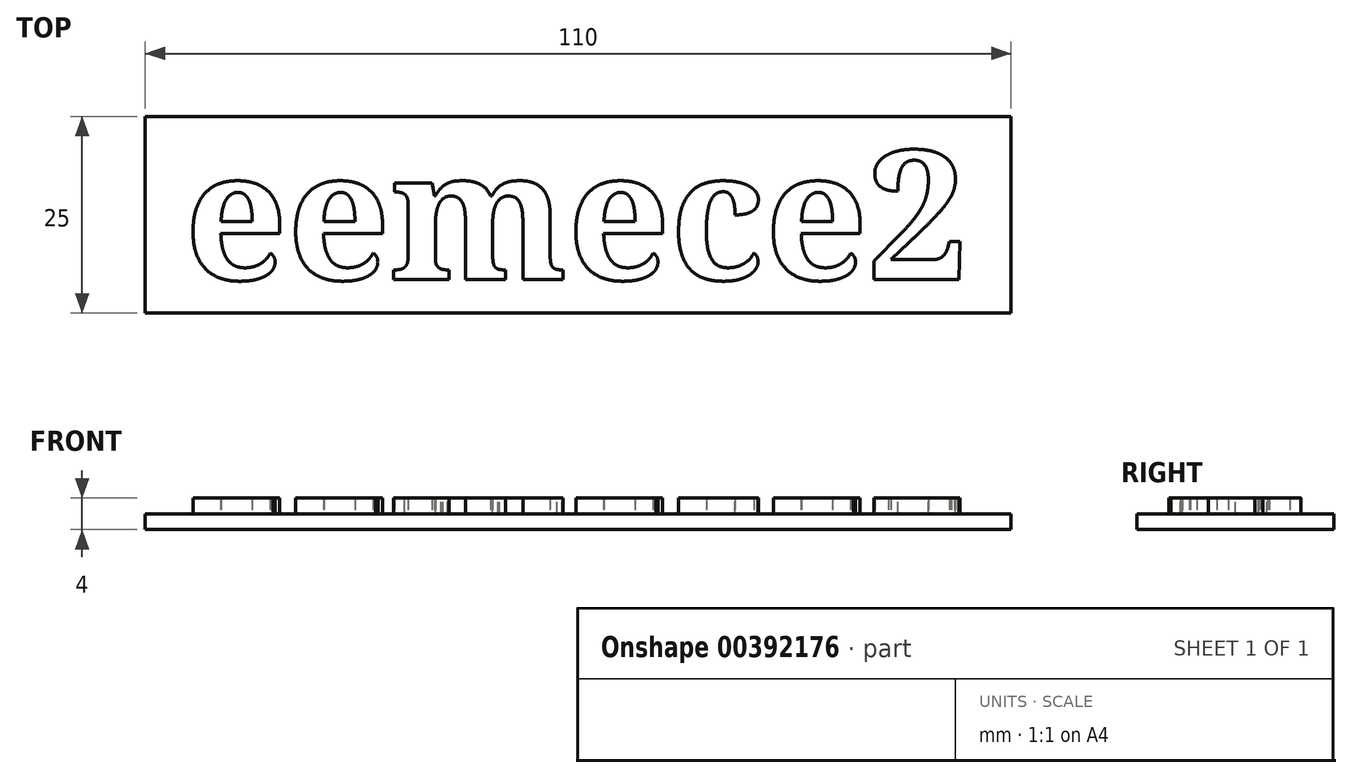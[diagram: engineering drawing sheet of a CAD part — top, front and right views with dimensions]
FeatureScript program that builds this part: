
annotation { "Feature Type Name" : "Feature", "Feature Type Description" : "" }
export const myFeature = defineFeature(function(context is Context, id is Id, definition is map)
    precondition{}
    {
        {
            var Q0;
            Q0=qCreatedBy(makeId("Top.planeOp"),FACE);
            var sketch = newSketch(context, id + "F0", { "sketchPlane" : qUnion([Q0])});
            skLineSegment(sketch, "E0.bottom", {"start": v(-55, 12.5) * mm, "end": v(55, 12.5) * mm});
            skLineSegment(sketch, "E0.top", {"start": v(-55, -12.5) * mm, "end": v(55, -12.5) * mm});
            skLineSegment(sketch, "E0.left", {"start": v(-55, 12.5) * mm, "end": v(-55, -12.5) * mm});
            skLineSegment(sketch, "E0.right", {"start": v(55, 12.5) * mm, "end": v(55, -12.5) * mm});
            skSolve(sketch);
        }
        {
            var Q0;
            Q0 = qSketchRegion(id + "F0", true);
            extrude(context, id + "F1", {"entities" : qUnion([Q0]), "depth" : 2 * mm});
        }
        {
            var Q0;
            Q0=makeQuery(id+"F1.opExtrude","CAP_FACE",FACE,{"disambiguationData":[OSD([sQuery(id+"F0.wireOp",EDGE,"E0.bottom"),sQuery(id+"F0.wireOp",EDGE,"E0.top"),sQuery(id+"F0.wireOp",EDGE,"E0.left"),sQuery(id+"F0.wireOp",EDGE,"E0.right")])],"isStart":false});
            var sketch = newSketch(context, id + "F2", { "sketchPlane" : qUnion([Q0])});
            skText(sketch, "E1", { "text": "eemece2", "fontName": "NotoSerif-Bold.ttf"});
            const initialGuessF2  = {"E1": [-0.05, -0.00823, 1, 0, 0.01646]};
            skSetInitialGuess(sketch, initialGuessF2);
            skSolve(sketch);
        }
        {
            var Q0;
            Q0 = qSketchRegion(id + "F2", true);
            extrude(context, id + "F3", {"entities" : qUnion([Q0]), "operationType" : NewBodyOperationType.ADD, "depth" : 2 * mm});
        }
    });
